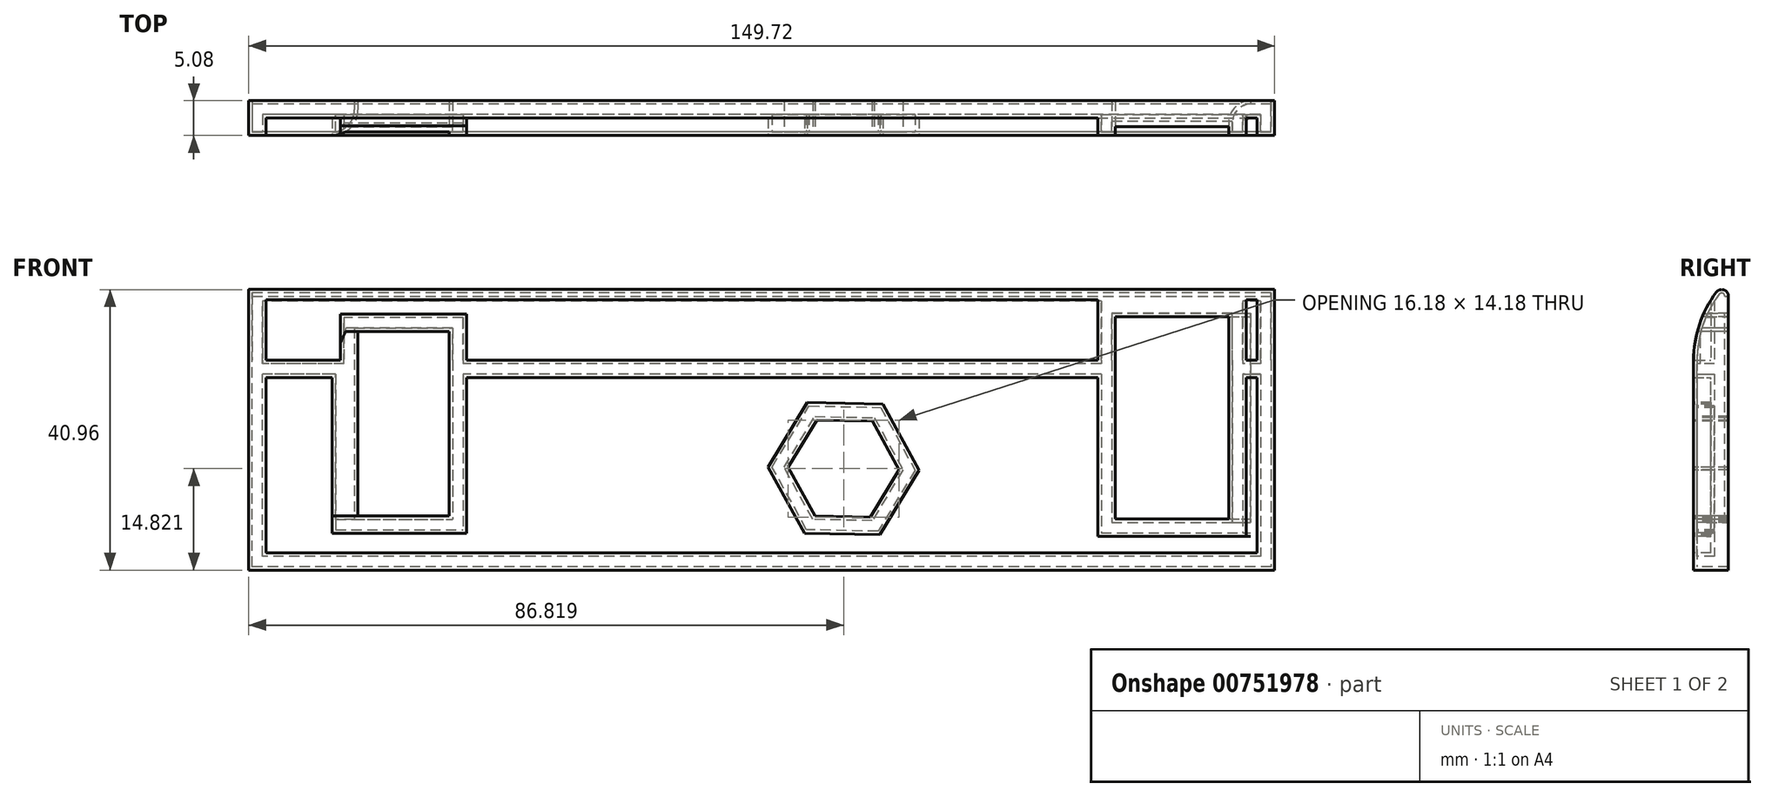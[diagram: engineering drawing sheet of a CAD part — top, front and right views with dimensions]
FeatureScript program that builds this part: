
annotation { "Feature Type Name" : "Feature", "Feature Type Description" : "" }
export const myFeature = defineFeature(function(context is Context, id is Id, definition is map)
    precondition{}
    {
        {
            var Q0;
            Q0=qCreatedBy(makeId("Front.planeOp"),FACE);
            var sketch = newSketch(context, id + "F0", { "sketchPlane" : qUnion([Q0])});
            skLineSegment(sketch, "E0", {"start": v(-116.9, 63.05) * mm, "end": v(32.82, 63.05) * mm});
            skLineSegment(sketch, "E1", {"start": v(32.82, 63.05) * mm, "end": v(32.82, 20.48) * mm});
            skLineSegment(sketch, "E2", {"start": v(32.82, 20.48) * mm, "end": v(-116.9, 20.48) * mm});
            skLineSegment(sketch, "E3", {"start": v(-116.9, 20.48) * mm, "end": v(-116.9, 63.05) * mm});
            skCircle(sketch, "E4.cCircle", {"center": v(-30.08, 35.3) * mm, "radius": 7 * mm, "construction": true});
            skLineSegment(sketch, "E4.0", {"start": v(-38.17, 35.47) * mm, "end": v(-33.98, 42.4) * mm});
            skLineSegment(sketch, "E4.1", {"start": v(-33.98, 42.4) * mm, "end": v(-25.89, 42.22) * mm});
            skLineSegment(sketch, "E4.2", {"start": v(-25.89, 42.22) * mm, "end": v(-22, 35.13) * mm});
            skLineSegment(sketch, "E4.3", {"start": v(-22, 35.13) * mm, "end": v(-26.19, 28.2) * mm});
            skLineSegment(sketch, "E4.4", {"start": v(-26.19, 28.2) * mm, "end": v(-34.27, 28.38) * mm});
            skLineSegment(sketch, "E4.5", {"start": v(-34.27, 28.38) * mm, "end": v(-38.17, 35.47) * mm});
            skPoint(sketch, "E4.0.midPoint", {"position": v(-36.07, 38.93) * mm});
            skLineSegment(sketch, "E5.bottom", {"start": v(-100.97, 55.3) * mm, "end": v(-87.65, 55.3) * mm});
            skLineSegment(sketch, "E5.top", {"start": v(-100.97, 28.38) * mm, "end": v(-87.65, 28.38) * mm});
            skLineSegment(sketch, "E5.left", {"start": v(-100.97, 55.3) * mm, "end": v(-100.97, 28.38) * mm});
            skLineSegment(sketch, "E5.right", {"start": v(-87.65, 55.3) * mm, "end": v(-87.65, 28.38) * mm});
            skLineSegment(sketch, "E6.bottom", {"start": v(9.56, 57.45) * mm, "end": v(26.15, 57.45) * mm});
            skLineSegment(sketch, "E6.top", {"start": v(9.56, 27.92) * mm, "end": v(26.15, 27.92) * mm});
            skLineSegment(sketch, "E6.left", {"start": v(9.56, 57.45) * mm, "end": v(9.56, 27.92) * mm});
            skLineSegment(sketch, "E6.right", {"start": v(26.15, 57.45) * mm, "end": v(26.15, 27.92) * mm});
            skSolve(sketch);
        }
        {
            var Q0;
            Q0=makeQuery(id+"F0.imprint","IMPRINT",FACE,{"disambiguationData":[TD([[makeQuery(id+"F0.imprint","IMPRINT",EDGE,{"derivedFrom":sQuery(id+"F0.wireOp",EDGE,"E0")}),-1.0]])]});
            extrude(context, id + "F1", {"entities" : qUnion([Q0]), "oppositeDirection" : true, "depth" : 5.08 * mm, "offsetDistance" : 25.4 * mm});
        }
        {
            var Q0;
            Q0=makeQuery(id+"F1.opExtrude","CAP_EDGE",EDGE,{"disambiguationData":[OSD([sQuery(id+"F0.wireOp",EDGE,"E0")])],"isStart":true});
            fillet(context, id + "F2", {"entities" : qUnion([Q0]), "radius" : 16.56 * mm, "tangentPropagation" : true, "allowEdgeOverflow" : false});
        }
        {
            var Q0;
            {var subQ0=sQuery(id+"F0.wireOp",EDGE,"E0");Q0=makeQuery(id+"F2.opFillet","BLEND_EDGE",EDGE,{"blendedFrom":[makeQuery(id+"F1.opExtrude","CAP_EDGE",EDGE,{"disambiguationData":[OSD([subQ0])],"isStart":true}),makeQuery(id+"F1.opExtrude","CAP_FACE",FACE,{"disambiguationData":[OSD([subQ0,sQuery(id+"F0.wireOp",EDGE,"E1"),sQuery(id+"F0.wireOp",EDGE,"E2"),sQuery(id+"F0.wireOp",EDGE,"E3"),sQuery(id+"F0.wireOp",EDGE,"E4.0"),sQuery(id+"F0.wireOp",EDGE,"E4.1"),sQuery(id+"F0.wireOp",EDGE,"E4.2"),sQuery(id+"F0.wireOp",EDGE,"E4.3"),sQuery(id+"F0.wireOp",EDGE,"E4.4"),sQuery(id+"F0.wireOp",EDGE,"E4.5")])],"isStart":false})],"blendedInto":[makeQuery(id+"F1.opExtrude","CAP_FACE",FACE,{"disambiguationData":[OSD([subQ0,sQuery(id+"F0.wireOp",EDGE,"E1"),sQuery(id+"F0.wireOp",EDGE,"E2"),sQuery(id+"F0.wireOp",EDGE,"E3"),sQuery(id+"F0.wireOp",EDGE,"E4.0"),sQuery(id+"F0.wireOp",EDGE,"E4.1"),sQuery(id+"F0.wireOp",EDGE,"E4.2"),sQuery(id+"F0.wireOp",EDGE,"E4.3"),sQuery(id+"F0.wireOp",EDGE,"E4.4"),sQuery(id+"F0.wireOp",EDGE,"E4.5")])],"isStart":false})]});}
            fillet(context, id + "F3", {"entities" : qUnion([Q0]), "radius" : 0.98 * mm, "tangentPropagation" : true, "allowEdgeOverflow" : false});
        }
        {
            var Q0;
            Q0=makeQuery(id+"F2.opFillet","BLEND_FACE",FACE,{"disambiguationData":[OSD([sQuery(id+"F0.wireOp",EDGE,"E0")])]});
            shell(context, id + "F4", {"entities" : qUnion([Q0]), "thickness" : 2.54 * mm});
        }
        {
            var Q0;
            Q0=makeQuery(id+"F1.opExtrude","CAP_EDGE",EDGE,{"disambiguationData":[OSD([sQuery(id+"F0.wireOp",EDGE,"E5.left")])],"isStart":true});
            var Q1;
            Q1=makeQuery(id+"F2.opFillet","BLEND_EDGE",EDGE,{"blendedFrom":[makeQuery(id+"F1.opExtrude","CAP_EDGE",EDGE,{"disambiguationData":[OSD([sQuery(id+"F0.wireOp",EDGE,"E0")])],"isStart":true}),makeQuery(id+"F1.opExtrude","SWEPT_FACE",FACE,{"disambiguationData":[OSD([sQuery(id+"F0.wireOp",EDGE,"E5.left")])]})],"blendedInto":[makeQuery(id+"F1.opExtrude","SWEPT_FACE",FACE,{"disambiguationData":[OSD([sQuery(id+"F0.wireOp",EDGE,"E5.left")])]})]});
            fillet(context, id + "F5", {"entities" : qUnion([Q0, Q1]), "radius" : 3.74 * mm, "tangentPropagation" : true, "allowEdgeOverflow" : false});
        }
        {
            var Q0;
            Q0=makeQuery(id+"F1.opExtrude","CAP_EDGE",EDGE,{"disambiguationData":[OSD([sQuery(id+"F0.wireOp",EDGE,"E6.right")])],"isStart":false});
            fillet(context, id + "F6", {"entities" : qUnion([Q0]), "radius" : 3.19 * mm, "tangentPropagation" : true, "allowEdgeOverflow" : false});
        }
        {
            var Q0;
            Q0=makeQuery(id+"F1.opExtrude","CAP_FACE",FACE,{"disambiguationData":[OSD([sQuery(id+"F0.wireOp",EDGE,"E0"),sQuery(id+"F0.wireOp",EDGE,"E1"),sQuery(id+"F0.wireOp",EDGE,"E2"),sQuery(id+"F0.wireOp",EDGE,"E3"),sQuery(id+"F0.wireOp",EDGE,"E4.0"),sQuery(id+"F0.wireOp",EDGE,"E4.1"),sQuery(id+"F0.wireOp",EDGE,"E4.2"),sQuery(id+"F0.wireOp",EDGE,"E4.3"),sQuery(id+"F0.wireOp",EDGE,"E4.4"),sQuery(id+"F0.wireOp",EDGE,"E4.5"),sQuery(id+"F0.wireOp",EDGE,"E5.bottom"),sQuery(id+"F0.wireOp",EDGE,"E5.top"),sQuery(id+"F0.wireOp",EDGE,"E5.left"),sQuery(id+"F0.wireOp",EDGE,"E5.right"),sQuery(id+"F0.wireOp",EDGE,"E6.bottom"),sQuery(id+"F0.wireOp",EDGE,"E6.top"),sQuery(id+"F0.wireOp",EDGE,"E6.left"),sQuery(id+"F0.wireOp",EDGE,"E6.right")])],"isStart":true});
            shell(context, id + "F7", {"entities" : qUnion([Q0]), "thickness" : 2.54 * mm});
        }
        {
            var Q0;
            Q0=makeQuery(id+"F1.opExtrude","CAP_FACE",FACE,{"disambiguationData":[OSD([sQuery(id+"F0.wireOp",EDGE,"E0"),sQuery(id+"F0.wireOp",EDGE,"E1"),sQuery(id+"F0.wireOp",EDGE,"E2"),sQuery(id+"F0.wireOp",EDGE,"E3"),sQuery(id+"F0.wireOp",EDGE,"E4.0"),sQuery(id+"F0.wireOp",EDGE,"E4.1"),sQuery(id+"F0.wireOp",EDGE,"E4.2"),sQuery(id+"F0.wireOp",EDGE,"E4.3"),sQuery(id+"F0.wireOp",EDGE,"E4.4"),sQuery(id+"F0.wireOp",EDGE,"E4.5"),sQuery(id+"F0.wireOp",EDGE,"E5.bottom"),sQuery(id+"F0.wireOp",EDGE,"E5.top"),sQuery(id+"F0.wireOp",EDGE,"E5.left"),sQuery(id+"F0.wireOp",EDGE,"E5.right"),sQuery(id+"F0.wireOp",EDGE,"E6.bottom"),sQuery(id+"F0.wireOp",EDGE,"E6.top"),sQuery(id+"F0.wireOp",EDGE,"E6.left"),sQuery(id+"F0.wireOp",EDGE,"E6.right")])],"isStart":false});
            shell(context, id + "F8", {"entities" : qUnion([Q0]), "thickness" : 0.5 * mm});
        }
    });
